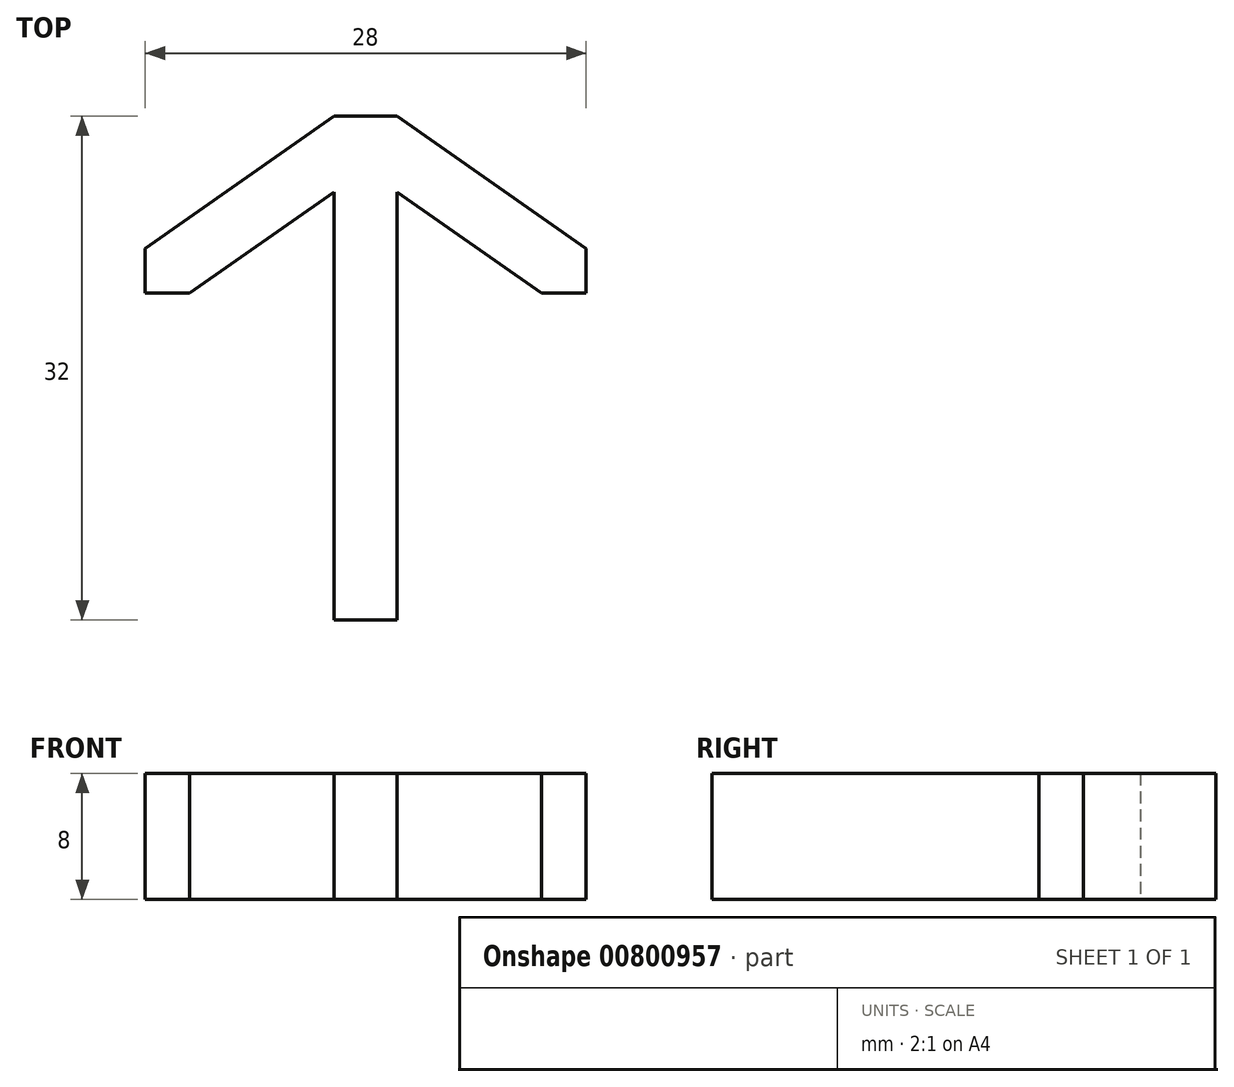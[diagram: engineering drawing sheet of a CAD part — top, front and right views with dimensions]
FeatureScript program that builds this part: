
annotation { "Feature Type Name" : "Feature", "Feature Type Description" : "" }
export const myFeature = defineFeature(function(context is Context, id is Id, definition is map)
    precondition{}
    {
        {
            var Q0;
            Q0=qCreatedBy(makeId("Top.planeOp"),FACE);
            var sketch = newSketch(context, id + "F0", { "sketchPlane" : qUnion([Q0])});
            skLineSegment(sketch, "E0", {"start": v(12, 0) * mm, "end": v(0, -8.4) * mm});
            skLineSegment(sketch, "E1", {"start": v(0, -8.4) * mm, "end": v(0, -11.23) * mm});
            skLineSegment(sketch, "E2", {"start": v(0, -11.23) * mm, "end": v(2.83, -11.23) * mm});
            skLineSegment(sketch, "E3", {"start": v(2.83, -11.23) * mm, "end": v(12, -4.8) * mm});
            skLineSegment(sketch, "E4", {"start": v(12, -4.8) * mm, "end": v(12, -32) * mm});
            skLineSegment(sketch, "E5", {"start": v(12, -32) * mm, "end": v(16, -32) * mm});
            skLineSegment(sketch, "E6", {"start": v(16, -32) * mm, "end": v(16, -4.8) * mm});
            skLineSegment(sketch, "E7", {"start": v(16, -4.8) * mm, "end": v(25.17, -11.23) * mm});
            skLineSegment(sketch, "E8", {"start": v(25.17, -11.23) * mm, "end": v(28, -11.23) * mm});
            skLineSegment(sketch, "E9", {"start": v(28, -11.23) * mm, "end": v(28, -8.4) * mm});
            skLineSegment(sketch, "E10", {"start": v(28, -8.4) * mm, "end": v(16, 0) * mm});
            skLineSegment(sketch, "E11", {"start": v(16, 0) * mm, "end": v(12, 0) * mm});
            skLineSegment(sketch, "E12", {"start": v(12, -4.8) * mm, "end": v(12, 0) * mm, "construction": true});
            skSolve(sketch);
        }
        {
            var Q0;
            Q0=makeQuery(id+"F0.imprint","IMPRINT",FACE,{"disambiguationData":[TD([[makeQuery(id+"F0.imprint","IMPRINT",EDGE,{"derivedFrom":sQuery(id+"F0.wireOp",EDGE,"E0")}),1.0]])]});
            extrude(context, id + "F1", {"entities" : qUnion([Q0]), "depth" : 8 * mm, "offsetDistance" : 25 * mm});
        }
    });
